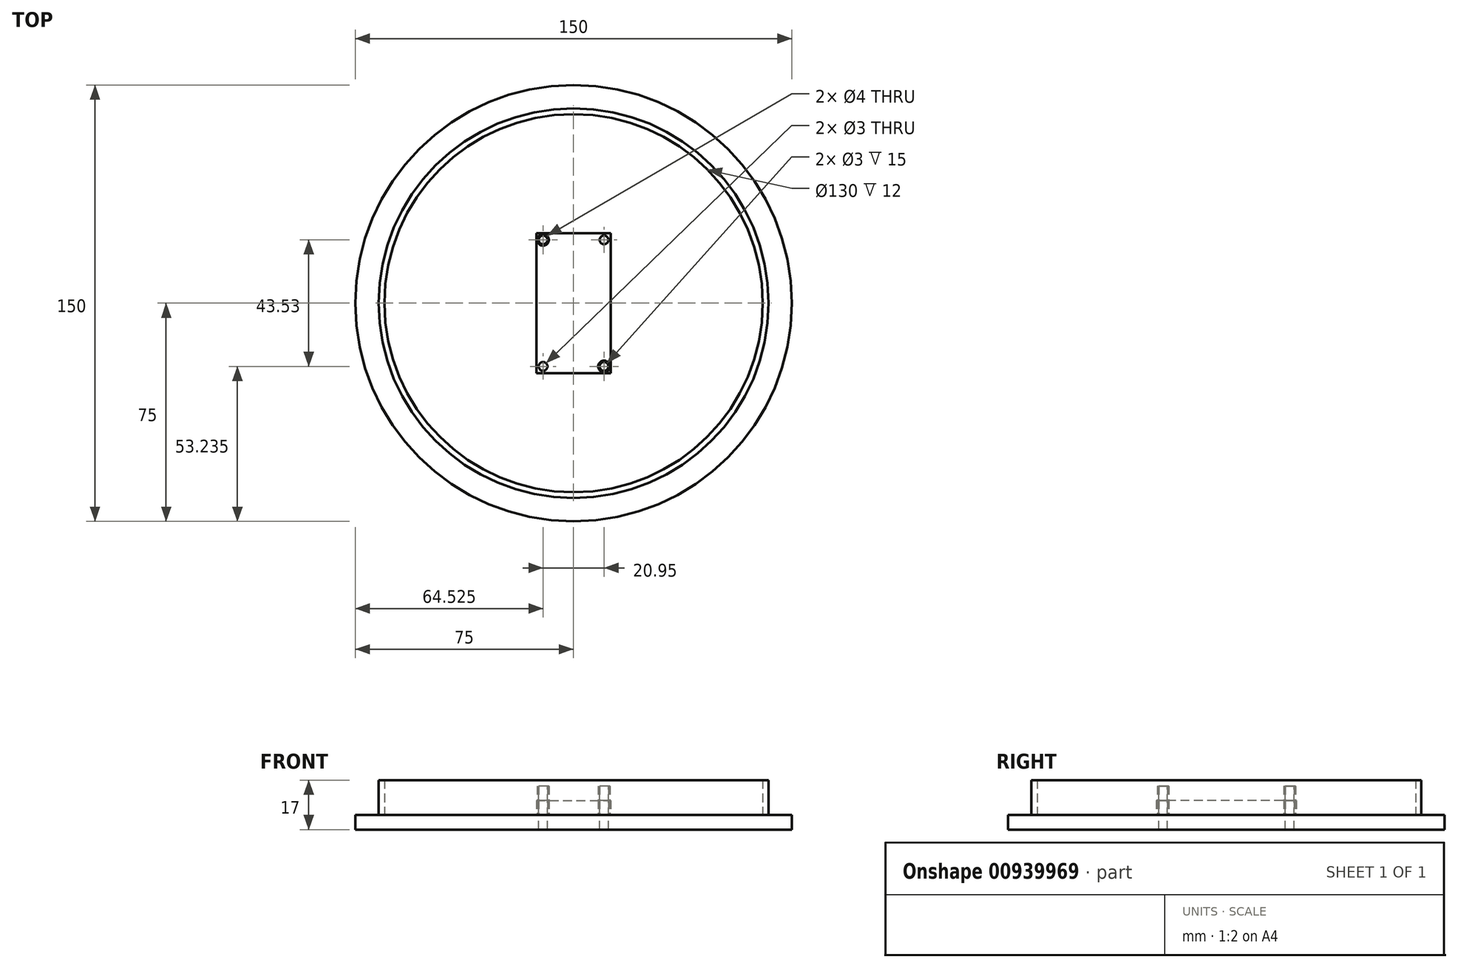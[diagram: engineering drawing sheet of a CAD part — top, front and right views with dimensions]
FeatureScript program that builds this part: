
annotation { "Feature Type Name" : "Feature", "Feature Type Description" : "" }
export const myFeature = defineFeature(function(context is Context, id is Id, definition is map)
    precondition{}
    {
        {
            assignVariable(context, id + "F0", {"name" : "nodemcuHeight", "anyValue" : 5});
        }
        {
            var Q0;
            Q0=qCreatedBy(makeId("Top.planeOp"),FACE);
            var sketch = newSketch(context, id + "F1", { "sketchPlane" : qUnion([Q0])});
            skCircle(sketch, "E0", {"center": v(0, 0) * mm, "radius": 75 * mm});
            skCircle(sketch, "E1.0", {"center": v(0, 0) * mm, "radius": 65 * mm});
            skLineSegment(sketch, "E2.bottom", {"start": v(-12.78, 24.07) * mm, "end": v(12.78, 24.07) * mm});
            skLineSegment(sketch, "E2.top", {"start": v(-12.78, -24.07) * mm, "end": v(12.79, -24.08) * mm});
            skLineSegment(sketch, "E2.left", {"start": v(-12.79, 24.07) * mm, "end": v(-12.78, -24.07) * mm});
            skLineSegment(sketch, "E2.right", {"start": v(12.78, 24.07) * mm, "end": v(12.79, -24.08) * mm});
            skPoint(sketch, "E3", {"position": v(0, 24.07) * mm});
            skPoint(sketch, "E4", {"position": v(-12.79, 0) * mm});
            skCircle(sketch, "E5", {"center": v(10.47, 21.76) * mm, "radius": 1.5 * mm});
            skCircle(sketch, "E6.0", {"center": v(10.47, 21.76) * mm, "radius": 2 * mm});
            skPoint(sketch, "E7", {"position": v(10.47, 23.26) * mm});
            skPoint(sketch, "E8", {"position": v(11.97, 21.76) * mm});
            skPoint(sketch, "E9", {"position": v(10.47, 24.07) * mm});
            skPoint(sketch, "E10", {"position": v(12.78, 21.76) * mm});
            skLineSegment(sketch, "E11", {"start": v(0, 24.07) * mm, "end": v(0, -24.07) * mm, "construction": true});
            skLineSegment(sketch, "E12", {"start": v(-12.79, 0) * mm, "end": v(12.79, 0) * mm, "construction": true});
            skCircle(sketch, "E13.0", {"center": v(0, 0) * mm, "radius": 67 * mm});
            skPoint(sketch, "E14", {"position": v(0, 67) * mm});
            skLineSegment(sketch, "E15", {"start": v(0, 67) * mm, "end": v(0, 24.07) * mm, "construction": true});
            skCircle(sketch, "E16.MirrorC", {"center": v(-10.47, 21.76) * mm, "radius": 2 * mm});
            skCircle(sketch, "E17.MirrorC", {"center": v(-10.47, 21.76) * mm, "radius": 1.5 * mm});
            skPoint(sketch, "E18.MirrorP", {"position": v(-10.47, 23.26) * mm});
            skPoint(sketch, "E19.MirrorP", {"position": v(-11.97, 21.76) * mm});
            skPoint(sketch, "E20.MirrorP", {"position": v(-10.47, 24.07) * mm});
            skPoint(sketch, "E21.MirrorP", {"position": v(-12.79, 21.76) * mm});
            skCircle(sketch, "E22.MirrorC", {"center": v(10.47, -21.77) * mm, "radius": 2 * mm});
            skCircle(sketch, "E23.MirrorC", {"center": v(10.47, -21.77) * mm, "radius": 1.5 * mm});
            skPoint(sketch, "E24.MirrorP", {"position": v(11.97, -21.77) * mm});
            skPoint(sketch, "E25.MirrorP", {"position": v(10.47, -23.27) * mm});
            skPoint(sketch, "E26.MirrorP", {"position": v(12.78, -21.77) * mm});
            skPoint(sketch, "E27.MirrorP", {"position": v(10.47, -24.08) * mm});
            skCircle(sketch, "E28.MirrorC", {"center": v(-10.47, -21.77) * mm, "radius": 2 * mm});
            skPoint(sketch, "E29.MirrorP", {"position": v(-11.97, -21.77) * mm});
            skCircle(sketch, "E30.MirrorC", {"center": v(-10.47, -21.77) * mm, "radius": 1.5 * mm});
            skPoint(sketch, "E31.MirrorP", {"position": v(-10.47, -24.08) * mm});
            skPoint(sketch, "E32.MirrorP", {"position": v(-10.47, -23.27) * mm});
            skPoint(sketch, "E33.MirrorP", {"position": v(-12.78, -21.77) * mm});
            skSolve(sketch);
        }
        {
            var Q0;
            Q0=makeQuery(id+"F1.imprint","IMPRINT",FACE,{"disambiguationData":[TD([[makeQuery(id+"F1.imprint","IMPRINT",EDGE,{"derivedFrom":sQuery(id+"F1.wireOp",EDGE,"E2.bottom")}),-1.0]])]});
            var Q1;
            Q1=makeQuery(id+"F1.imprint","IMPRINT",FACE,{"disambiguationData":[TD([[makeQuery(id+"F1.imprint","IMPRINT",EDGE,{"derivedFrom":sQuery(id+"F1.wireOp",EDGE,"E0")}),1.0]])]});
            var Q2;
            Q2=makeQuery(id+"F1.imprint","IMPRINT",FACE,{"disambiguationData":[TD([[makeQuery(id+"F1.imprint","IMPRINT",EDGE,{"derivedFrom":sQuery(id+"F1.wireOp",EDGE,"E1.0")}),-1.0]])]});
            var Q3;
            Q3=makeQuery(id+"F1.imprint","IMPRINT",FACE,{"disambiguationData":[TD([[makeQuery(id+"F1.imprint","IMPRINT",EDGE,{"derivedFrom":sQuery(id+"F1.wireOp",EDGE,"E1.0")}),1.0]])]});
            var Q4;
            Q4=makeQuery(id+"F1.imprint","IMPRINT",FACE,{"disambiguationData":[TD([[makeQuery(id+"F1.imprint","IMPRINT",EDGE,{"derivedFrom":sQuery(id+"F1.wireOp",EDGE,"E16.MirrorC")}),-1.0]])]});
            var Q5;
            Q5=makeQuery(id+"F1.imprint","IMPRINT",FACE,{"disambiguationData":[TD([[makeQuery(id+"F1.imprint","IMPRINT",EDGE,{"derivedFrom":sQuery(id+"F1.wireOp",EDGE,"E28.MirrorC")}),1.0]])]});
            var Q6;
            Q6=makeQuery(id+"F1.imprint","IMPRINT",FACE,{"disambiguationData":[TD([[makeQuery(id+"F1.imprint","IMPRINT",EDGE,{"derivedFrom":sQuery(id+"F1.wireOp",EDGE,"E22.MirrorC")}),-1.0]])]});
            var Q7;
            Q7=makeQuery(id+"F1.imprint","IMPRINT",FACE,{"disambiguationData":[TD([[makeQuery(id+"F1.imprint","IMPRINT",EDGE,{"derivedFrom":sQuery(id+"F1.wireOp",EDGE,"E5")}),-1.0]])]});
            var Q8;
            Q8=makeQuery(id+"F1.imprint","IMPRINT",FACE,{"disambiguationData":[TD([[makeQuery(id+"F1.imprint","IMPRINT",EDGE,{"derivedFrom":sQuery(id+"F1.wireOp",EDGE,"E23.MirrorC")}),-1.0]])]});
            var Q9;
            Q9=makeQuery(id+"F1.imprint","IMPRINT",FACE,{"disambiguationData":[TD([[makeQuery(id+"F1.imprint","IMPRINT",EDGE,{"derivedFrom":sQuery(id+"F1.wireOp",EDGE,"E17.MirrorC")}),-1.0]])]});
            var Q10;
            Q10=makeQuery(id+"F1.imprint","IMPRINT",FACE,{"disambiguationData":[TD([[makeQuery(id+"F1.imprint","IMPRINT",EDGE,{"derivedFrom":sQuery(id+"F1.wireOp",EDGE,"E5")}),1.0]])]});
            var Q11;
            Q11=makeQuery(id+"F1.imprint","IMPRINT",FACE,{"disambiguationData":[TD([[makeQuery(id+"F1.imprint","IMPRINT",EDGE,{"derivedFrom":sQuery(id+"F1.wireOp",EDGE,"E30.MirrorC")}),1.0]])]});
            extrude(context, id + "F2", {"entities" : qUnion([Q0, Q1, Q2, Q3, Q4, Q5, Q6, Q7, Q8, Q9, Q10, Q11]), "depth" : -5 * mm, "offsetDistance" : 25 * mm});
        }
        {
            var Q0;
            Q0=makeQuery(id+"F1.imprint","IMPRINT",FACE,{"disambiguationData":[TD([[makeQuery(id+"F1.imprint","IMPRINT",EDGE,{"derivedFrom":sQuery(id+"F1.wireOp",EDGE,"E5")}),1.0]])]});
            var Q1;
            Q1=makeQuery(id+"F1.imprint","IMPRINT",FACE,{"disambiguationData":[TD([[makeQuery(id+"F1.imprint","IMPRINT",EDGE,{"derivedFrom":sQuery(id+"F1.wireOp",EDGE,"E17.MirrorC")}),-1.0]])]});
            var Q2;
            Q2=makeQuery(id+"F1.imprint","IMPRINT",FACE,{"disambiguationData":[TD([[makeQuery(id+"F1.imprint","IMPRINT",EDGE,{"derivedFrom":sQuery(id+"F1.wireOp",EDGE,"E23.MirrorC")}),-1.0]])]});
            var Q3;
            Q3=makeQuery(id+"F1.imprint","IMPRINT",FACE,{"disambiguationData":[TD([[makeQuery(id+"F1.imprint","IMPRINT",EDGE,{"derivedFrom":sQuery(id+"F1.wireOp",EDGE,"E30.MirrorC")}),1.0]])]});
            extrude(context, id + "F3", {"entities" : qUnion([Q0, Q1, Q2, Q3]), "operationType" : NewBodyOperationType.ADD, "depth" : (getVariable(context, 'nodemcuHeight') + 5) * mm, "offsetDistance" : 25 * mm});
        }
        {
            var Q0;
            Q0=makeQuery(id+"F1.imprint","IMPRINT",FACE,{"disambiguationData":[TD([[makeQuery(id+"F1.imprint","IMPRINT",EDGE,{"derivedFrom":sQuery(id+"F1.wireOp",EDGE,"E5")}),-1.0]])]});
            var Q1;
            Q1=makeQuery(id+"F1.imprint","IMPRINT",FACE,{"disambiguationData":[TD([[makeQuery(id+"F1.imprint","IMPRINT",EDGE,{"derivedFrom":sQuery(id+"F1.wireOp",EDGE,"E16.MirrorC")}),-1.0]])]});
            var Q2;
            Q2=makeQuery(id+"F1.imprint","IMPRINT",FACE,{"disambiguationData":[TD([[makeQuery(id+"F1.imprint","IMPRINT",EDGE,{"derivedFrom":sQuery(id+"F1.wireOp",EDGE,"E28.MirrorC")}),1.0]])]});
            var Q3;
            Q3=makeQuery(id+"F1.imprint","IMPRINT",FACE,{"disambiguationData":[TD([[makeQuery(id+"F1.imprint","IMPRINT",EDGE,{"derivedFrom":sQuery(id+"F1.wireOp",EDGE,"E22.MirrorC")}),-1.0]])]});
            extrude(context, id + "F4", {"entities" : qUnion([Q0, Q1, Q2, Q3]), "depth" : (getVariable(context, 'nodemcuHeight')) * mm, "offsetDistance" : 25 * mm});
        }
        {
            var Q0;
            Q0=makeQuery(id+"F1.imprint","IMPRINT",FACE,{"disambiguationData":[TD([[makeQuery(id+"F1.imprint","IMPRINT",EDGE,{"derivedFrom":sQuery(id+"F1.wireOp",EDGE,"E1.0")}),-1.0]])]});
            extrude(context, id + "F5", {"entities" : qUnion([Q0]), "operationType" : NewBodyOperationType.ADD, "depth" : 12 * mm, "offsetDistance" : 25 * mm});
        }
    });
